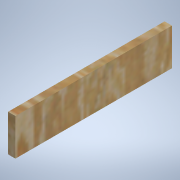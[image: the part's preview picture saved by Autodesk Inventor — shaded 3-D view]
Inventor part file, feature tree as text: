
AUTODESK INVENTOR PART (.ipt)
format: ipt  version: 2021.1 (Build 251245000, 245)  size: 145,408 bytes
history: native  units: mm
features: extrude x3, sketch x3, other x3, reference x1
ambient origin geometry x8: Origin, YZ Plane, XZ Plane, XY Plane, X Axis, Y Axis, Z Axis, Center Point
bodies: Solid1 (feature_tree)
feature tree (10):
  extrude  "Extrusion1"  Depth=270.0mm TaperAngle=0.0deg
  extrude  "Extrusion2"  Depth=12.7mm TaperAngle=0.0deg
  extrude  "Extrusion3"  [1 undecoded]
  sketch  "Sketch1"  dims[d0=6.35mm d1=270.0mm d2=0.0mm]
  reference  "Reference1"
  sketch  "Sketch2"  dims[d3=6.35mm d4=0.0mm d5=12.7mm d6=0.0mm]
  sketch  "Sketch3"
  other  "<userpath>\Documents\Kerbal Kontroller\Design\Final\Inventor\Final.iam"
  other  "Final.iam"
  other  "Bottom:1"
note: 1 required parameter value undecoded (feature->parameter linkage not recoverable at this tier; creation-order binding heuristic only, values carry confidence <= 0.55)
